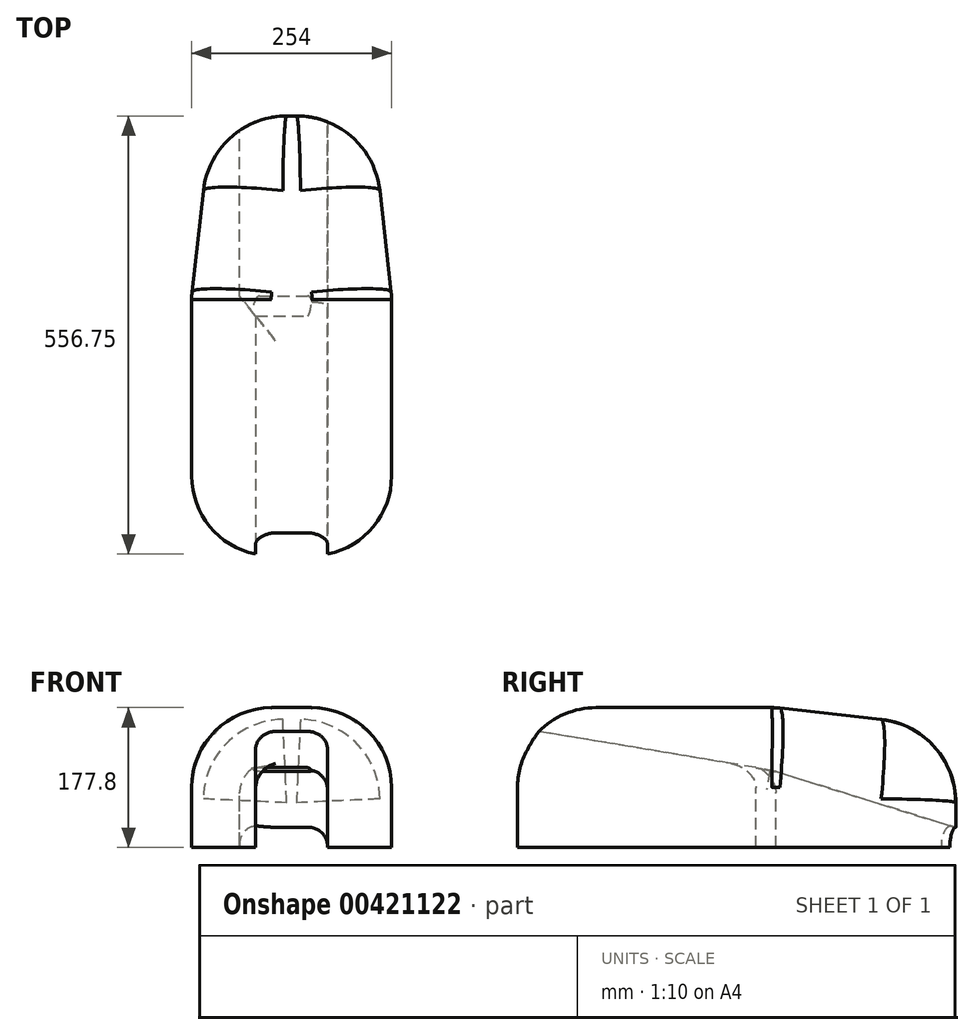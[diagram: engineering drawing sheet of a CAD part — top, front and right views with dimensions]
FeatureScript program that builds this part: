
annotation { "Feature Type Name" : "Feature", "Feature Type Description" : "" }
export const myFeature = defineFeature(function(context is Context, id is Id, definition is map)
    precondition{}
    {
        {
            var Q0;
            Q0=qCreatedBy(makeId("Front.planeOp"),FACE);
            var sketch = newSketch(context, id + "F0", { "sketchPlane" : qUnion([Q0])});
            skLineSegment(sketch, "E0.bottom", {"start": v(-127, 0) * mm, "end": v(-45.72, 0) * mm});
            skLineSegment(sketch, "E0.top", {"start": v(-127, 177.8) * mm, "end": v(127, 177.8) * mm});
            skLineSegment(sketch, "E0.left", {"start": v(-127, 0) * mm, "end": v(-127, 177.8) * mm});
            skLineSegment(sketch, "E0.right", {"start": v(127, 0) * mm, "end": v(127, 177.8) * mm});
            skLineSegment(sketch, "E1.top", {"start": v(-45.72, 152.4) * mm, "end": v(45.72, 152.4) * mm});
            skLineSegment(sketch, "E1.left", {"start": v(-45.72, 0) * mm, "end": v(-45.72, 152.4) * mm});
            skLineSegment(sketch, "E1.right", {"start": v(45.72, 0) * mm, "end": v(45.72, 152.4) * mm});
            skLineSegment(sketch, "E2.trimOffspring", {"start": v(45.72, 0) * mm, "end": v(127, 0) * mm});
            skSolve(sketch);
        }
        {
            var Q0;
            Q0=qCreatedBy(makeId("Front.planeOp"),FACE);
            cPlane(context, id + "F1", {"entities" : qUnion([Q0]), "cplaneType" : CPlaneType.OFFSET, "offset" : 304.8 * mm, "oppositeDirection" : true, "width" : 152.4 * mm, "height" : 152.4 * mm});
        }
        {
            var Q0;
            Q0=qCreatedBy(id+"F1.planeOp",FACE);
            var sketch = newSketch(context, id + "F2", { "sketchPlane" : qUnion([Q0])});
            skLineSegment(sketch, "E3.bottom", {"start": v(-127, 0) * mm, "end": v(-45.72, 0) * mm});
            skLineSegment(sketch, "E3.top", {"start": v(-127, 177.8) * mm, "end": v(127, 177.8) * mm});
            skLineSegment(sketch, "E3.left", {"start": v(-127, 0) * mm, "end": v(-127, 177.8) * mm});
            skLineSegment(sketch, "E3.right", {"start": v(127, 0) * mm, "end": v(127, 177.8) * mm});
            skLineSegment(sketch, "E4.top", {"start": v(-45.72, 101.6) * mm, "end": v(45.72, 101.6) * mm});
            skLineSegment(sketch, "E4.left", {"start": v(-45.72, 0) * mm, "end": v(-45.72, 101.6) * mm});
            skLineSegment(sketch, "E4.right", {"start": v(45.72, 0) * mm, "end": v(45.72, 101.6) * mm});
            skLineSegment(sketch, "E5.trimOffspring", {"start": v(45.72, 0) * mm, "end": v(127, 0) * mm});
            skSolve(sketch);
        }
        {
            var Q0;
            Q0=qCreatedBy(makeId("Front.planeOp"),FACE);
            cPlane(context, id + "F3", {"entities" : qUnion([Q0]), "cplaneType" : CPlaneType.OFFSET, "offset" : 330.2 * mm, "oppositeDirection" : true, "width" : 152.4 * mm, "height" : 152.4 * mm});
        }
        {
            var Q0;
            Q0=qCreatedBy(id+"F3.planeOp",FACE);
            var sketch = newSketch(context, id + "F4", { "sketchPlane" : qUnion([Q0])});
            skLineSegment(sketch, "E6.bottom", {"start": v(-127, 0) * mm, "end": v(-66.04, 0) * mm});
            skLineSegment(sketch, "E6.top", {"start": v(-127, 177.8) * mm, "end": v(127, 177.8) * mm});
            skLineSegment(sketch, "E6.left", {"start": v(-127, 0) * mm, "end": v(-127, 177.8) * mm});
            skLineSegment(sketch, "E6.right", {"start": v(127, 0) * mm, "end": v(127, 177.8) * mm});
            skLineSegment(sketch, "E7.top", {"start": v(-66.04, 96.52) * mm, "end": v(45.72, 96.52) * mm});
            skLineSegment(sketch, "E7.left", {"start": v(-66.04, 0) * mm, "end": v(-66.04, 96.52) * mm});
            skLineSegment(sketch, "E7.right", {"start": v(45.72, 0) * mm, "end": v(45.72, 96.52) * mm});
            skLineSegment(sketch, "E8.trimOffspring", {"start": v(45.72, 0) * mm, "end": v(127, 0) * mm});
            skSolve(sketch);
        }
        {
            var Q0;
            Q0=qCreatedBy(makeId("Front.planeOp"),FACE);
            cPlane(context, id + "F5", {"entities" : qUnion([Q0]), "cplaneType" : CPlaneType.OFFSET, "offset" : 558.8 * mm, "oppositeDirection" : true, "width" : 152.4 * mm, "height" : 152.4 * mm});
        }
        {
            var Q0;
            Q0=qCreatedBy(id+"F5.planeOp",FACE);
            var sketch = newSketch(context, id + "F6", { "sketchPlane" : qUnion([Q0])});
            skLineSegment(sketch, "E9.bottom", {"start": v(-101.6, 0) * mm, "end": v(-66.04, 0) * mm});
            skLineSegment(sketch, "E9.top", {"start": v(-101.6, 152.4) * mm, "end": v(101.6, 152.4) * mm});
            skLineSegment(sketch, "E9.left", {"start": v(-101.6, 0) * mm, "end": v(-101.6, 152.4) * mm});
            skLineSegment(sketch, "E9.right", {"start": v(101.6, 0) * mm, "end": v(101.6, 152.4) * mm});
            skLineSegment(sketch, "E10.top", {"start": v(-66.04, 25.4) * mm, "end": v(45.72, 25.4) * mm});
            skLineSegment(sketch, "E10.left", {"start": v(-66.04, 0) * mm, "end": v(-66.04, 25.4) * mm});
            skLineSegment(sketch, "E10.right", {"start": v(45.72, 0) * mm, "end": v(45.72, 25.4) * mm});
            skLineSegment(sketch, "E11.trimOffspring", {"start": v(45.72, 0) * mm, "end": v(101.6, 0) * mm});
            skSolve(sketch);
        }
        {
            var Q0;
            Q0 = qSketchRegion(id + "F2", true);
            var Q1;
            Q1 = qSketchRegion(id + "F4", true);
            loft(context, id + "F7", {"sheetProfilesArray" : [{ "sheetProfileEntities" : qUnion([Q0]) }, { "sheetProfileEntities" : qUnion([Q1]) }]});
        }
        {
            var Q1;
            Q1 = qSketchRegion(id + "F4", true);
            var Q2;
            Q2 = qSketchRegion(id + "F6", true);
            loft(context, id + "F8", {"operationType" : NewBodyOperationType.ADD, "sheetProfilesArray" : [{ "sheetProfileEntities" : qUnion([Q1]) }, { "sheetProfileEntities" : qUnion([Q2]) }]});
        }
        {
            var Q1;
            Q1 = qSketchRegion(id + "F2", true);
            var Q2;
            Q2 = qSketchRegion(id + "F0", true);
            loft(context, id + "F9", {"operationType" : NewBodyOperationType.ADD, "sheetProfilesArray" : [{ "sheetProfileEntities" : qUnion([Q1]) }, { "sheetProfileEntities" : qUnion([Q2]) }]});
        }
        {
            var Q0;
            {var subQ0=sQuery(id+"F2.wireOp",EDGE,"E3.right");var subQ1=sQuery(id+"F2.wireOp",EDGE,"E3.top");Q0=makeQuery(id+"F9.boolean.opBoolean","MERGE",EDGE,{"derivedFrom":[makeQuery(id+"F7.opLoft","SWEPT_EDGE",EDGE,{"disambiguationData":[OSD([subQ1,subQ0,sQuery(id+"F4.wireOp",EDGE,"E6.top"),sQuery(id+"F4.wireOp",EDGE,"E6.right")])]}),makeQuery(id+"F9.opLoft","SWEPT_EDGE",EDGE,{"disambiguationData":[OSD([sQuery(id+"F0.wireOp",EDGE,"E0.top"),sQuery(id+"F0.wireOp",EDGE,"E0.right"),subQ1,subQ0])]})]});}
            var Q1;
            Q1=makeQuery(id+"F8.opLoft","SWEPT_EDGE",EDGE,{"disambiguationData":[OSD([sQuery(id+"F4.wireOp",EDGE,"E6.top"),sQuery(id+"F4.wireOp",EDGE,"E6.right"),sQuery(id+"F6.wireOp",EDGE,"E9.top"),sQuery(id+"F6.wireOp",EDGE,"E9.right")])]});
            var Q2;
            {var subQ0=sQuery(id+"F2.wireOp",EDGE,"E3.left");var subQ1=sQuery(id+"F2.wireOp",EDGE,"E3.top");Q2=makeQuery(id+"F9.boolean.opBoolean","MERGE",EDGE,{"derivedFrom":[makeQuery(id+"F7.opLoft","SWEPT_EDGE",EDGE,{"disambiguationData":[OSD([subQ1,subQ0,sQuery(id+"F4.wireOp",EDGE,"E6.top"),sQuery(id+"F4.wireOp",EDGE,"E6.left")])]}),makeQuery(id+"F9.opLoft","SWEPT_EDGE",EDGE,{"disambiguationData":[OSD([sQuery(id+"F0.wireOp",EDGE,"E0.top"),sQuery(id+"F0.wireOp",EDGE,"E0.left"),subQ1,subQ0])]})]});}
            var Q3;
            Q3=makeQuery(id+"F8.opLoft","SWEPT_EDGE",EDGE,{"disambiguationData":[OSD([sQuery(id+"F4.wireOp",EDGE,"E6.top"),sQuery(id+"F4.wireOp",EDGE,"E6.left"),sQuery(id+"F6.wireOp",EDGE,"E9.top"),sQuery(id+"F6.wireOp",EDGE,"E9.left")])]});
            fillet(context, id + "F10", {"entities" : qUnion([Q0, Q1, Q2, Q3]), "radius" : 101.6 * mm, "tangentPropagation" : true, "allowEdgeOverflow" : false});
        }
        {
            var Q0;
            {var subQ0=sQuery(id+"F4.wireOp",EDGE,"E8.trimOffspring");var subQ1=sQuery(id+"F4.wireOp",EDGE,"E6.right");var subQ2=sQuery(id+"F4.wireOp",EDGE,"E6.top");Q0=makeQuery(id+"F8.boolean.opBoolean","MERGE",EDGE,{"derivedFrom":[makeQuery(id+"F7.opLoft","MID_CAP_EDGE",EDGE,{"disambiguationData":[OSD([subQ2,subQ1,subQ0])],"capPos":1.0}),makeQuery(id+"F8.opLoft","MID_CAP_EDGE",EDGE,{"disambiguationData":[OSD([subQ2,subQ1,subQ0])],"capPos":0.0})]});}
            var Q1;
            {var subQ0=sQuery(id+"F2.wireOp",EDGE,"E3.right");var subQ1=sQuery(id+"F2.wireOp",EDGE,"E3.top");var subQ2=sQuery(id+"F4.wireOp",EDGE,"E6.right");var subQ3=sQuery(id+"F4.wireOp",EDGE,"E6.top");Q1=makeQuery(id+"F10.opFillet","BLEND_EDGE",EDGE,{"blendedFrom":[makeQuery(id+"F8.opLoft","SWEPT_EDGE",EDGE,{"disambiguationData":[OSD([subQ3,subQ2,sQuery(id+"F6.wireOp",EDGE,"E9.top"),sQuery(id+"F6.wireOp",EDGE,"E9.right")])]}),makeQuery(id+"F9.boolean.opBoolean","MERGE",EDGE,{"derivedFrom":[makeQuery(id+"F7.opLoft","SWEPT_EDGE",EDGE,{"disambiguationData":[OSD([subQ1,subQ0,subQ3,subQ2])]}),makeQuery(id+"F9.opLoft","SWEPT_EDGE",EDGE,{"disambiguationData":[OSD([sQuery(id+"F0.wireOp",EDGE,"E0.top"),sQuery(id+"F0.wireOp",EDGE,"E0.right"),subQ1,subQ0])]})]})],"blendedInto":[]});}
            var Q2;
            {var subQ0=sQuery(id+"F4.wireOp",EDGE,"E6.right");var subQ1=sQuery(id+"F4.wireOp",EDGE,"E6.left");var subQ2=sQuery(id+"F4.wireOp",EDGE,"E6.top");Q2=makeQuery(id+"F8.boolean.opBoolean","MERGE",EDGE,{"derivedFrom":[makeQuery(id+"F7.opLoft","MID_CAP_EDGE",EDGE,{"disambiguationData":[OSD([subQ2,subQ1,subQ0])],"capPos":1.0}),makeQuery(id+"F8.opLoft","MID_CAP_EDGE",EDGE,{"disambiguationData":[OSD([subQ2,subQ1,subQ0])],"capPos":0.0})]});}
            var Q3;
            {var subQ0=sQuery(id+"F2.wireOp",EDGE,"E3.left");var subQ1=sQuery(id+"F2.wireOp",EDGE,"E3.top");var subQ2=sQuery(id+"F4.wireOp",EDGE,"E6.left");var subQ3=sQuery(id+"F4.wireOp",EDGE,"E6.top");Q3=makeQuery(id+"F10.opFillet","BLEND_EDGE",EDGE,{"blendedFrom":[makeQuery(id+"F8.opLoft","SWEPT_EDGE",EDGE,{"disambiguationData":[OSD([subQ3,subQ2,sQuery(id+"F6.wireOp",EDGE,"E9.top"),sQuery(id+"F6.wireOp",EDGE,"E9.left")])]}),makeQuery(id+"F9.boolean.opBoolean","MERGE",EDGE,{"derivedFrom":[makeQuery(id+"F7.opLoft","SWEPT_EDGE",EDGE,{"disambiguationData":[OSD([subQ1,subQ0,subQ3,subQ2])]}),makeQuery(id+"F9.opLoft","SWEPT_EDGE",EDGE,{"disambiguationData":[OSD([sQuery(id+"F0.wireOp",EDGE,"E0.top"),sQuery(id+"F0.wireOp",EDGE,"E0.left"),subQ1,subQ0])]})]})],"blendedInto":[]});}
            var Q4;
            {var subQ0=sQuery(id+"F4.wireOp",EDGE,"E6.left");var subQ1=sQuery(id+"F4.wireOp",EDGE,"E6.top");var subQ2=sQuery(id+"F4.wireOp",EDGE,"E6.bottom");Q4=makeQuery(id+"F8.boolean.opBoolean","MERGE",EDGE,{"derivedFrom":[makeQuery(id+"F7.opLoft","MID_CAP_EDGE",EDGE,{"disambiguationData":[OSD([subQ2,subQ1,subQ0])],"capPos":1.0}),makeQuery(id+"F8.opLoft","MID_CAP_EDGE",EDGE,{"disambiguationData":[OSD([subQ2,subQ1,subQ0])],"capPos":0.0})]});}
            fillet(context, id + "F11", {"entities" : qUnion([Q0, Q1, Q2, Q3, Q4]), "radius" : 88.9 * mm, "tangentPropagation" : true, "allowEdgeOverflow" : false});
        }
        {
            var Q0;
            Q0=makeQuery(id+"F9.opLoft","MID_CAP_EDGE",EDGE,{"disambiguationData":[OSD([sQuery(id+"F0.wireOp",EDGE,"E0.top"),sQuery(id+"F0.wireOp",EDGE,"E0.left"),sQuery(id+"F0.wireOp",EDGE,"E0.right")])],"capPos":1.0});
            var Q1;
            {var subQ0=sQuery(id+"F0.wireOp",EDGE,"E0.right");var subQ1=sQuery(id+"F0.wireOp",EDGE,"E0.top");var subQ2=sQuery(id+"F2.wireOp",EDGE,"E3.right");var subQ3=sQuery(id+"F2.wireOp",EDGE,"E3.top");Q1=makeQuery(id+"F10.opFillet","BLEND_EDGE",EDGE,{"blendedFrom":[makeQuery(id+"F9.boolean.opBoolean","MERGE",EDGE,{"derivedFrom":[makeQuery(id+"F7.opLoft","SWEPT_EDGE",EDGE,{"disambiguationData":[OSD([subQ3,subQ2,sQuery(id+"F4.wireOp",EDGE,"E6.top"),sQuery(id+"F4.wireOp",EDGE,"E6.right")])]}),makeQuery(id+"F9.opLoft","SWEPT_EDGE",EDGE,{"disambiguationData":[OSD([subQ1,subQ0,subQ3,subQ2])]})]}),makeQuery(id+"F9.opLoft","CAP_FACE",FACE,{"disambiguationData":[OSD([makeQuery(id+"F0.imprint","IMPRINT",FACE,{"disambiguationData":[TD([[makeQuery(id+"F0.imprint","IMPRINT",EDGE,{"derivedFrom":sQuery(id+"F0.wireOp",EDGE,"E0.bottom")}),1.0]])]})])],"isStart":true})],"blendedInto":[makeQuery(id+"F9.opLoft","CAP_FACE",FACE,{"disambiguationData":[OSD([makeQuery(id+"F0.imprint","IMPRINT",FACE,{"disambiguationData":[TD([[makeQuery(id+"F0.imprint","IMPRINT",EDGE,{"derivedFrom":sQuery(id+"F0.wireOp",EDGE,"E0.bottom")}),1.0]])]})])],"isStart":true})]});}
            var Q2;
            Q2=makeQuery(id+"F9.opLoft","MID_CAP_EDGE",EDGE,{"disambiguationData":[OSD([sQuery(id+"F0.wireOp",EDGE,"E0.top"),sQuery(id+"F0.wireOp",EDGE,"E0.right"),sQuery(id+"F0.wireOp",EDGE,"E2.trimOffspring")])],"capPos":1.0});
            var Q3;
            {var subQ0=sQuery(id+"F0.wireOp",EDGE,"E0.left");var subQ1=sQuery(id+"F0.wireOp",EDGE,"E0.top");var subQ2=sQuery(id+"F2.wireOp",EDGE,"E3.left");var subQ3=sQuery(id+"F2.wireOp",EDGE,"E3.top");Q3=makeQuery(id+"F10.opFillet","BLEND_EDGE",EDGE,{"blendedFrom":[makeQuery(id+"F9.boolean.opBoolean","MERGE",EDGE,{"derivedFrom":[makeQuery(id+"F7.opLoft","SWEPT_EDGE",EDGE,{"disambiguationData":[OSD([subQ3,subQ2,sQuery(id+"F4.wireOp",EDGE,"E6.top"),sQuery(id+"F4.wireOp",EDGE,"E6.left")])]}),makeQuery(id+"F9.opLoft","SWEPT_EDGE",EDGE,{"disambiguationData":[OSD([subQ1,subQ0,subQ3,subQ2])]})]}),makeQuery(id+"F9.opLoft","CAP_FACE",FACE,{"disambiguationData":[OSD([makeQuery(id+"F0.imprint","IMPRINT",FACE,{"disambiguationData":[TD([[makeQuery(id+"F0.imprint","IMPRINT",EDGE,{"derivedFrom":sQuery(id+"F0.wireOp",EDGE,"E0.bottom")}),1.0]])]})])],"isStart":true})],"blendedInto":[makeQuery(id+"F9.opLoft","CAP_FACE",FACE,{"disambiguationData":[OSD([makeQuery(id+"F0.imprint","IMPRINT",FACE,{"disambiguationData":[TD([[makeQuery(id+"F0.imprint","IMPRINT",EDGE,{"derivedFrom":sQuery(id+"F0.wireOp",EDGE,"E0.bottom")}),1.0]])]})])],"isStart":true})]});}
            var Q4;
            Q4=makeQuery(id+"F9.opLoft","MID_CAP_EDGE",EDGE,{"disambiguationData":[OSD([sQuery(id+"F0.wireOp",EDGE,"E0.bottom"),sQuery(id+"F0.wireOp",EDGE,"E0.top"),sQuery(id+"F0.wireOp",EDGE,"E0.left")])],"capPos":1.0});
            fillet(context, id + "F12", {"entities" : qUnion([Q0, Q1, Q2, Q3, Q4]), "radius" : 101.6 * mm, "tangentPropagation" : true, "allowEdgeOverflow" : false});
        }
        {
            var Q0;
            {var subQ0=sQuery(id+"F6.wireOp",EDGE,"E9.right");var subQ1=sQuery(id+"F6.wireOp",EDGE,"E9.top");Q0=makeQuery(id+"F10.opFillet","BLEND_EDGE",EDGE,{"blendedFrom":[makeQuery(id+"F8.opLoft","SWEPT_EDGE",EDGE,{"disambiguationData":[OSD([sQuery(id+"F4.wireOp",EDGE,"E6.top"),sQuery(id+"F4.wireOp",EDGE,"E6.right"),subQ1,subQ0])]}),makeQuery(id+"F8.opLoft","CAP_FACE",FACE,{"disambiguationData":[OSD([makeQuery(id+"F6.imprint","IMPRINT",FACE,{"disambiguationData":[TD([[makeQuery(id+"F6.imprint","IMPRINT",EDGE,{"derivedFrom":sQuery(id+"F6.wireOp",EDGE,"E9.bottom")}),1.0]])]})])],"isStart":true})],"blendedInto":[makeQuery(id+"F8.opLoft","CAP_FACE",FACE,{"disambiguationData":[OSD([makeQuery(id+"F6.imprint","IMPRINT",FACE,{"disambiguationData":[TD([[makeQuery(id+"F6.imprint","IMPRINT",EDGE,{"derivedFrom":sQuery(id+"F6.wireOp",EDGE,"E9.bottom")}),1.0]])]})])],"isStart":true})]});}
            var Q1;
            Q1=makeQuery(id+"F8.opLoft","MID_CAP_EDGE",EDGE,{"disambiguationData":[OSD([sQuery(id+"F6.wireOp",EDGE,"E9.top"),sQuery(id+"F6.wireOp",EDGE,"E9.left"),sQuery(id+"F6.wireOp",EDGE,"E9.right")])],"capPos":1.0});
            var Q2;
            {var subQ0=sQuery(id+"F6.wireOp",EDGE,"E9.left");var subQ1=sQuery(id+"F6.wireOp",EDGE,"E9.top");Q2=makeQuery(id+"F10.opFillet","BLEND_EDGE",EDGE,{"blendedFrom":[makeQuery(id+"F8.opLoft","SWEPT_EDGE",EDGE,{"disambiguationData":[OSD([sQuery(id+"F4.wireOp",EDGE,"E6.top"),sQuery(id+"F4.wireOp",EDGE,"E6.left"),subQ1,subQ0])]}),makeQuery(id+"F8.opLoft","CAP_FACE",FACE,{"disambiguationData":[OSD([makeQuery(id+"F6.imprint","IMPRINT",FACE,{"disambiguationData":[TD([[makeQuery(id+"F6.imprint","IMPRINT",EDGE,{"derivedFrom":sQuery(id+"F6.wireOp",EDGE,"E9.bottom")}),1.0]])]})])],"isStart":true})],"blendedInto":[makeQuery(id+"F8.opLoft","CAP_FACE",FACE,{"disambiguationData":[OSD([makeQuery(id+"F6.imprint","IMPRINT",FACE,{"disambiguationData":[TD([[makeQuery(id+"F6.imprint","IMPRINT",EDGE,{"derivedFrom":sQuery(id+"F6.wireOp",EDGE,"E9.bottom")}),1.0]])]})])],"isStart":true})]});}
            fillet(context, id + "F13", {"entities" : qUnion([Q0, Q1, Q2]), "radius" : 106.68 * mm, "tangentPropagation" : true, "allowEdgeOverflow" : false});
        }
        {
            var Q0;
            Q0=makeQuery(id+"F9.opLoft","SWEPT_EDGE",EDGE,{"disambiguationData":[OSD([sQuery(id+"F0.wireOp",EDGE,"E1.top"),sQuery(id+"F0.wireOp",EDGE,"E1.right"),sQuery(id+"F2.wireOp",EDGE,"E4.top"),sQuery(id+"F2.wireOp",EDGE,"E4.right")])]});
            fillet(context, id + "F14", {"entities" : qUnion([Q0]), "radius" : 25.4 * mm, "tangentPropagation" : true, "allowEdgeOverflow" : false});
        }
        {
            var Q0;
            Q0=makeQuery(id+"F8.opLoft","SWEPT_EDGE",EDGE,{"disambiguationData":[OSD([sQuery(id+"F4.wireOp",EDGE,"E7.top"),sQuery(id+"F4.wireOp",EDGE,"E7.right"),sQuery(id+"F6.wireOp",EDGE,"E10.top"),sQuery(id+"F6.wireOp",EDGE,"E10.right")])]});
            var Q1;
            Q1=makeQuery(id+"F8.opLoft","SWEPT_EDGE",EDGE,{"disambiguationData":[OSD([sQuery(id+"F4.wireOp",EDGE,"E7.top"),sQuery(id+"F4.wireOp",EDGE,"E7.left"),sQuery(id+"F6.wireOp",EDGE,"E10.top"),sQuery(id+"F6.wireOp",EDGE,"E10.left")])]});
            var Q2;
            Q2=makeQuery(id+"F9.opLoft","SWEPT_EDGE",EDGE,{"disambiguationData":[OSD([sQuery(id+"F0.wireOp",EDGE,"E1.top"),sQuery(id+"F0.wireOp",EDGE,"E1.left"),sQuery(id+"F2.wireOp",EDGE,"E4.top"),sQuery(id+"F2.wireOp",EDGE,"E4.left")])]});
            fillet(context, id + "F15", {"entities" : qUnion([Q0, Q1, Q2]), "radius" : 25.4 * mm, "tangentPropagation" : true, "allowEdgeOverflow" : false});
        }
    });
